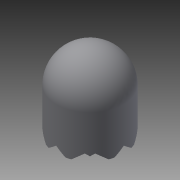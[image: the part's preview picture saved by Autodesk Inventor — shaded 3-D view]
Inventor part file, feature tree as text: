
AUTODESK INVENTOR PART (.ipt)
format: ipt  version: 2015 (Build 190159000, 159)  size: 196,608 bytes
history: native  units: in
note: dims shown in document units (in); Inventor stores cm internally (conversion verified against a paired STEP export)
features: extrude x2, sketch x2, fillet x1, projected_geometry x1
ambient origin geometry x8: Origin, YZ Plane, XZ Plane, XY Plane, X Axis, Y Axis, Z Axis, Center Point
bodies: Solid1 (feature_tree)
feature tree (6):
  extrude  "Extrusion1"  Depth=0.625in
  fillet  "Fillet1"  Radius=1.0in
  extrude  "Extrusion2"  Depth=0.5in
  sketch  "Sketch1"  dims[d5=1.0in d6=0.625in d7=1.0in]
  sketch  "Sketch2"  dims[d8=0.0625in d9=0.125in d10=0.1in d11=0.125in d12=0.0625in d13=0.125in d14=0.1in d15=0.125in d16=0.1in d17=0.125in d18=0.125in d19=1.0in d20=0.0in d21=0.5in d22=1.0in d23=0.625in d24=1.0in d25=0.0625in d26=0.125in d27=0.1in d28=0.125in d29=0.0625in d30=0.125in d31=0.1in d32=0.125in d33=0.1in d34=0.125in d35=0.125in d36=1.0in d37=0.0in]
  projected_geometry  "Projected Loop1"
